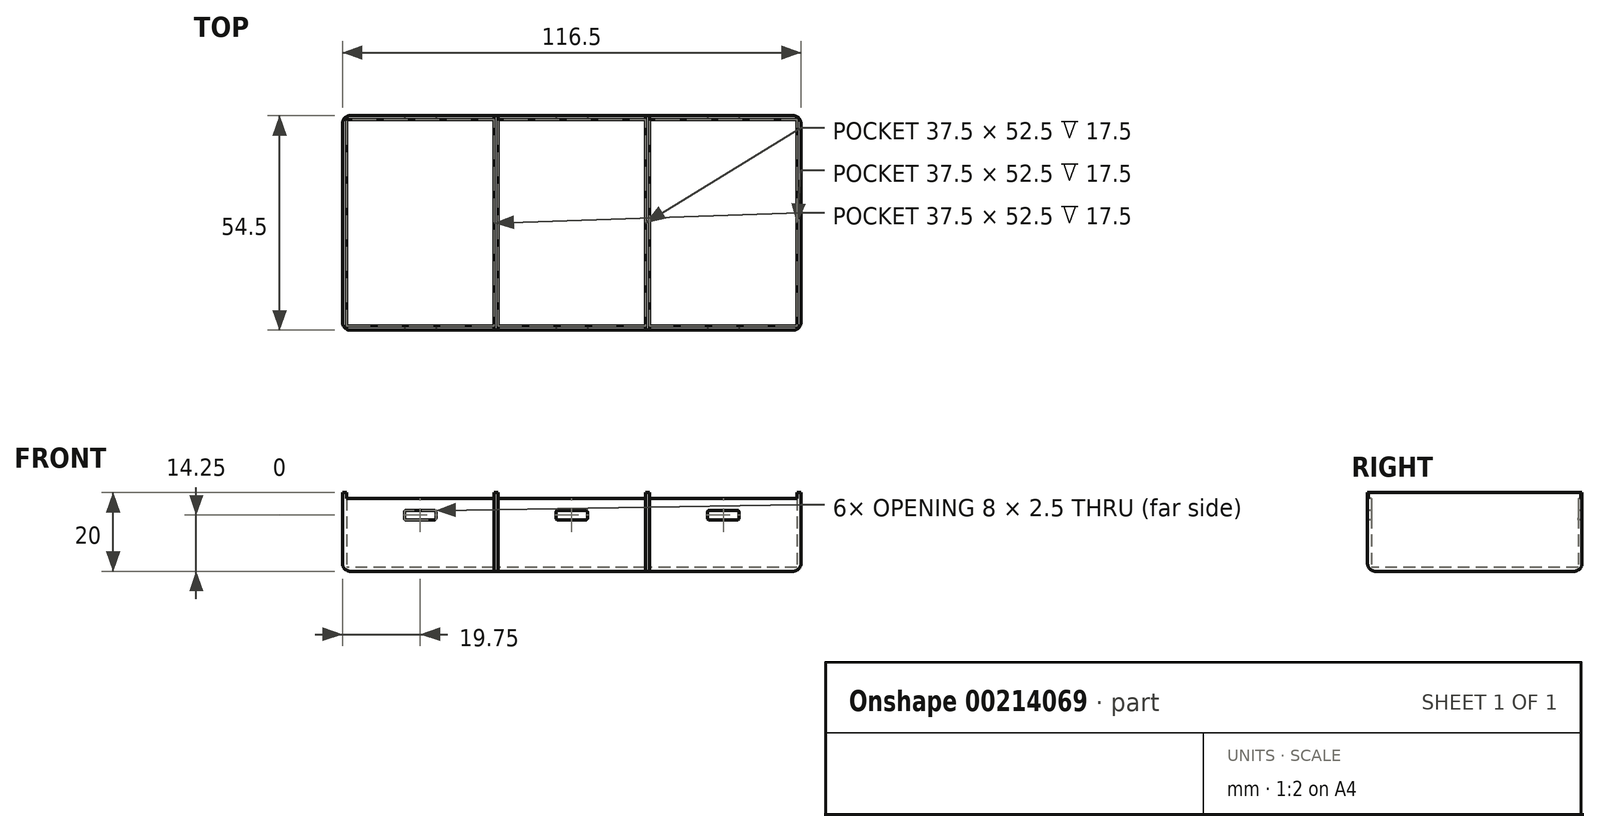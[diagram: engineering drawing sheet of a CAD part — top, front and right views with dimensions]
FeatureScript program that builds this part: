
annotation { "Feature Type Name" : "Feature", "Feature Type Description" : "" }
export const myFeature = defineFeature(function(context is Context, id is Id, definition is map)
    precondition{}
    {
        {
            var Q0;
            Q0=qCreatedBy(makeId("Top.planeOp"),FACE);
            var sketch = newSketch(context, id + "F0", { "sketchPlane" : qUnion([Q0])});
            skLineSegment(sketch, "E0.bottom", {"start": v(18.75, 26.25) * mm, "end": v(-18.75, 26.25) * mm});
            skLineSegment(sketch, "E0.top", {"start": v(18.75, -26.25) * mm, "end": v(-18.75, -26.25) * mm});
            skLineSegment(sketch, "E0.left", {"start": v(18.75, 26.25) * mm, "end": v(18.75, -26.25) * mm});
            skLineSegment(sketch, "E0.right", {"start": v(-18.75, 26.25) * mm, "end": v(-18.75, -26.25) * mm});
            skPoint(sketch, "E0.middle", {"position": v(0, 0) * mm});
            skLineSegment(sketch, "E1.bottom", {"start": v(19.75, 27.25) * mm, "end": v(-19.75, 27.25) * mm});
            skLineSegment(sketch, "E1.top", {"start": v(19.75, -27.25) * mm, "end": v(-19.75, -27.25) * mm});
            skLineSegment(sketch, "E1.left", {"start": v(19.75, 27.25) * mm, "end": v(19.75, -27.25) * mm});
            skLineSegment(sketch, "E1.right", {"start": v(-19.75, 27.25) * mm, "end": v(-19.75, -27.25) * mm});
            skLineSegment(sketch, "E2", {"start": v(18.75, 26.25) * mm, "end": v(18.75, 27.25) * mm});
            skLineSegment(sketch, "E3", {"start": v(18.75, -26.25) * mm, "end": v(18.75, -27.25) * mm});
            skLineSegment(sketch, "E4", {"start": v(-18.75, 26.25) * mm, "end": v(-18.75, 27.25) * mm});
            skLineSegment(sketch, "E5", {"start": v(-18.75, -26.25) * mm, "end": v(-18.75, -27.25) * mm});
            skSolve(sketch);
        }
        {
            var Q0;
            Q0=makeQuery(id+"F0.imprint","IMPRINT",FACE,{"disambiguationData":[TD([[makeQuery(id+"F0.imprint","IMPRINT",EDGE,{"derivedFrom":sQuery(id+"F0.wireOp",EDGE,"E0.bottom")}),1.0]])]});
            extrude(context, id + "F1", {"entities" : qUnion([Q0]), "depth" : 1 * mm});
        }
        {
            var Q0;
            Q0=makeQuery(id+"F0.imprint","IMPRINT",FACE,{"disambiguationData":[TD([[makeQuery(id+"F0.imprint","IMPRINT",EDGE,{"derivedFrom":sQuery(id+"F0.wireOp",EDGE,"E0.bottom")}),-1.0]])]});
            var Q1;
            Q1=makeQuery(id+"F0.imprint","IMPRINT",FACE,{"disambiguationData":[TD([[makeQuery(id+"F0.imprint","IMPRINT",EDGE,{"derivedFrom":sQuery(id+"F0.wireOp",EDGE,"E0.top")}),1.0]])]});
            extrude(context, id + "F2", {"entities" : qUnion([Q0, Q1]), "operationType" : NewBodyOperationType.ADD, "depth" : 18.5 * mm});
        }
        {
            var Q0;
            Q0=makeQuery(id+"F2.opExtrude","SWEPT_FACE",FACE,{"disambiguationData":[OSD([sQuery(id+"F0.wireOp",EDGE,"E1.top")])]});
            var sketch = newSketch(context, id + "F3", { "sketchPlane" : qUnion([Q0])});
            skLineSegment(sketch, "E6.bottom", {"start": v(3.5, 15.5) * mm, "end": v(-3.5, 15.5) * mm});
            skLineSegment(sketch, "E6.top", {"start": v(3.5, 13) * mm, "end": v(-3.5, 13) * mm});
            skLineSegment(sketch, "E6.left", {"start": v(4, 15) * mm, "end": v(4, 13.5) * mm});
            skLineSegment(sketch, "E6.right", {"start": v(-4, 15) * mm, "end": v(-4, 13.5) * mm});
            skPoint(sketch, "E6.middle", {"position": v(0, 14.25) * mm});
            skPoint(sketch, "E7.visualSharp", {"position": v(-4, 15.5) * mm});
            skArc(sketch, "E7.filletArc", {"start": v(-3.5, 15.5) * mm, "mid": v(-3.85, 15.35) * mm, "end": v(-4, 15) * mm});
            skPoint(sketch, "E8.visualSharp", {"position": v(-4, 13) * mm});
            skArc(sketch, "E8.filletArc", {"start": v(-4, 13.5) * mm, "mid": v(-3.85, 13.15) * mm, "end": v(-3.5, 13) * mm});
            skPoint(sketch, "E9.visualSharp", {"position": v(4, 13) * mm});
            skArc(sketch, "E9.filletArc", {"start": v(3.5, 13) * mm, "mid": v(3.85, 13.15) * mm, "end": v(4, 13.5) * mm});
            skPoint(sketch, "E10.visualSharp", {"position": v(4, 15.5) * mm});
            skArc(sketch, "E10.filletArc", {"start": v(4, 15) * mm, "mid": v(3.85, 15.35) * mm, "end": v(3.5, 15.5) * mm});
            skSolve(sketch);
        }
        {
            var Q0;
            Q0=makeQuery(id+"F3.imprint","IMPRINT",FACE,{"disambiguationData":[TD([[makeQuery(id+"F3.imprint","IMPRINT",EDGE,{"derivedFrom":sQuery(id+"F3.wireOp",EDGE,"E6.bottom")}),1.0]])]});
            extrude(context, id + "F4", {"entities" : qUnion([Q0]), "operationType" : NewBodyOperationType.REMOVE, "oppositeDirection" : true, "depth" : 60 * mm});
        }
        {
            var Q0;
            Q0=makeQuery(id+"F0.imprint","IMPRINT",FACE,{"disambiguationData":[TD([[makeQuery(id+"F0.imprint","IMPRINT",EDGE,{"derivedFrom":sQuery(id+"F0.wireOp",EDGE,"E0.right")}),-1.0]])]});
            var Q1;
            Q1=makeQuery(id+"F0.imprint","IMPRINT",FACE,{"disambiguationData":[TD([[makeQuery(id+"F0.imprint","IMPRINT",EDGE,{"derivedFrom":sQuery(id+"F0.wireOp",EDGE,"E0.left")}),1.0]])]});
            extrude(context, id + "F5", {"entities" : qUnion([Q0, Q1]), "operationType" : NewBodyOperationType.ADD, "depth" : 20 * mm});
        }
        {
            var Q0;
            Q0=makeQuery(id+"F1.opExtrude","SWEPT_BODY",BODY,{"disambiguationData":[OSD([sQuery(id+"F0.wireOp",EDGE,"E0.bottom"),sQuery(id+"F0.wireOp",EDGE,"E0.top"),sQuery(id+"F0.wireOp",EDGE,"E0.left"),sQuery(id+"F0.wireOp",EDGE,"E0.right")])]});
            transform(context, id + "F6", {"entities" : qUnion([Q0]), "transformType" : TransformType.TRANSLATION_3D, "dx" : 38.5 * mm, "dy" : 0 * mm, "dz" : 0 * mm, "makeCopy" : true});
        }
        {
            var Q0;
            Q0=makeQuery(id+"F6.opPattern","COPY",BODY,{"derivedFrom":makeQuery(id+"F1.opExtrude","SWEPT_BODY",BODY,{"disambiguationData":[OSD([sQuery(id+"F0.wireOp",EDGE,"E0.bottom"),sQuery(id+"F0.wireOp",EDGE,"E0.top"),sQuery(id+"F0.wireOp",EDGE,"E0.left"),sQuery(id+"F0.wireOp",EDGE,"E0.right")])]}),"instanceName":"1"});
            transform(context, id + "F7", {"entities" : qUnion([Q0]), "transformType" : TransformType.TRANSLATION_3D, "dx" : 38.5 * mm, "dy" : 0 * mm, "dz" : 0 * mm, "makeCopy" : true});
        }
        {
            var Q0;
            Q0=makeQuery(id+"F5.opExtrude","SWEPT_EDGE",EDGE,{"disambiguationData":[OSD([sQuery(id+"F0.wireOp",EDGE,"E1.top"),sQuery(id+"F0.wireOp",EDGE,"E1.right")])]});
            var Q1;
            Q1=makeQuery(id+"F5.opExtrude","SWEPT_EDGE",EDGE,{"disambiguationData":[OSD([sQuery(id+"F0.wireOp",EDGE,"E1.bottom"),sQuery(id+"F0.wireOp",EDGE,"E1.right")])]});
            var Q2;
            Q2=makeQuery(id+"F7.opPattern","COPY",EDGE,{"derivedFrom":makeQuery(id+"F6.opPattern","COPY",EDGE,{"derivedFrom":makeQuery(id+"F5.opExtrude","SWEPT_EDGE",EDGE,{"disambiguationData":[OSD([sQuery(id+"F0.wireOp",EDGE,"E1.top"),sQuery(id+"F0.wireOp",EDGE,"E1.left")])]}),"instanceName":"1"}),"instanceName":"1"});
            var Q3;
            Q3=makeQuery(id+"F7.opPattern","COPY",EDGE,{"derivedFrom":makeQuery(id+"F6.opPattern","COPY",EDGE,{"derivedFrom":makeQuery(id+"F5.opExtrude","SWEPT_EDGE",EDGE,{"disambiguationData":[OSD([sQuery(id+"F0.wireOp",EDGE,"E1.bottom"),sQuery(id+"F0.wireOp",EDGE,"E1.left")])]}),"instanceName":"1"}),"instanceName":"1"});
            fillet(context, id + "F8", {"entities" : qUnion([Q0, Q1, Q2, Q3]), "radius" : 2 * mm, "tangentPropagation" : true, "allowEdgeOverflow" : false});
        }
        {
            var Q0;
            {var subQ0=sQuery(id+"F0.wireOp",EDGE,"E1.top");Q0=makeQuery(id+"F5.boolean.opBoolean","MERGE",EDGE,{"derivedFrom":[makeQuery(id+"F2.opExtrude","CAP_EDGE",EDGE,{"disambiguationData":[OSD([subQ0])],"isStart":true}),makeQuery(id+"F5.opExtrude","CAP_EDGE",EDGE,{"disambiguationData":[OSD([subQ0]),TDD([makeQuery(id+"F0.imprint","IMPRINT",EDGE,{"disambiguationData":[TD([[makeQuery(id+"F0.imprint","INTERSECT",VERTEX,{"derivedFrom":[subQ0,sQuery(id+"F0.wireOp",EDGE,"E1.left")]}),-1.0]])],"derivedFrom":subQ0})])],"isStart":true}),makeQuery(id+"F5.opExtrude","CAP_EDGE",EDGE,{"disambiguationData":[OSD([subQ0]),TDD([makeQuery(id+"F0.imprint","IMPRINT",EDGE,{"disambiguationData":[TD([[makeQuery(id+"F0.imprint","INTERSECT",VERTEX,{"derivedFrom":[subQ0,sQuery(id+"F0.wireOp",EDGE,"E1.right")]}),1.0]])],"derivedFrom":subQ0})])],"isStart":true})]});}
            var Q1;
            Q1=makeQuery(id+"F5.opExtrude","CAP_EDGE",EDGE,{"disambiguationData":[OSD([sQuery(id+"F0.wireOp",EDGE,"E1.right")])],"isStart":true});
            var Q2;
            {var subQ0=sQuery(id+"F0.wireOp",EDGE,"E1.top");Q2=makeQuery(id+"F6.opPattern","COPY",EDGE,{"derivedFrom":makeQuery(id+"F5.boolean.opBoolean","MERGE",EDGE,{"derivedFrom":[makeQuery(id+"F2.opExtrude","CAP_EDGE",EDGE,{"disambiguationData":[OSD([subQ0])],"isStart":true}),makeQuery(id+"F5.opExtrude","CAP_EDGE",EDGE,{"disambiguationData":[OSD([subQ0]),TDD([makeQuery(id+"F0.imprint","IMPRINT",EDGE,{"disambiguationData":[TD([[makeQuery(id+"F0.imprint","INTERSECT",VERTEX,{"derivedFrom":[subQ0,sQuery(id+"F0.wireOp",EDGE,"E1.left")]}),-1.0]])],"derivedFrom":subQ0})])],"isStart":true}),makeQuery(id+"F5.opExtrude","CAP_EDGE",EDGE,{"disambiguationData":[OSD([subQ0]),TDD([makeQuery(id+"F0.imprint","IMPRINT",EDGE,{"disambiguationData":[TD([[makeQuery(id+"F0.imprint","INTERSECT",VERTEX,{"derivedFrom":[subQ0,sQuery(id+"F0.wireOp",EDGE,"E1.right")]}),1.0]])],"derivedFrom":subQ0})])],"isStart":true})]}),"instanceName":"1"});}
            var Q3;
            {var subQ0=sQuery(id+"F0.wireOp",EDGE,"E1.top");Q3=makeQuery(id+"F7.opPattern","COPY",EDGE,{"derivedFrom":makeQuery(id+"F6.opPattern","COPY",EDGE,{"derivedFrom":makeQuery(id+"F5.boolean.opBoolean","MERGE",EDGE,{"derivedFrom":[makeQuery(id+"F2.opExtrude","CAP_EDGE",EDGE,{"disambiguationData":[OSD([subQ0])],"isStart":true}),makeQuery(id+"F5.opExtrude","CAP_EDGE",EDGE,{"disambiguationData":[OSD([subQ0]),TDD([makeQuery(id+"F0.imprint","IMPRINT",EDGE,{"disambiguationData":[TD([[makeQuery(id+"F0.imprint","INTERSECT",VERTEX,{"derivedFrom":[subQ0,sQuery(id+"F0.wireOp",EDGE,"E1.left")]}),-1.0]])],"derivedFrom":subQ0})])],"isStart":true}),makeQuery(id+"F5.opExtrude","CAP_EDGE",EDGE,{"disambiguationData":[OSD([subQ0]),TDD([makeQuery(id+"F0.imprint","IMPRINT",EDGE,{"disambiguationData":[TD([[makeQuery(id+"F0.imprint","INTERSECT",VERTEX,{"derivedFrom":[subQ0,sQuery(id+"F0.wireOp",EDGE,"E1.right")]}),1.0]])],"derivedFrom":subQ0})])],"isStart":true})]}),"instanceName":"1"}),"instanceName":"1"});}
            var Q4;
            {var subQ0=sQuery(id+"F0.wireOp",EDGE,"E1.bottom");Q4=makeQuery(id+"F6.opPattern","COPY",EDGE,{"derivedFrom":makeQuery(id+"F5.boolean.opBoolean","MERGE",EDGE,{"derivedFrom":[makeQuery(id+"F2.opExtrude","CAP_EDGE",EDGE,{"disambiguationData":[OSD([subQ0])],"isStart":true}),makeQuery(id+"F5.opExtrude","CAP_EDGE",EDGE,{"disambiguationData":[OSD([subQ0]),TDD([makeQuery(id+"F0.imprint","IMPRINT",EDGE,{"disambiguationData":[TD([[makeQuery(id+"F0.imprint","INTERSECT",VERTEX,{"derivedFrom":[subQ0,sQuery(id+"F0.wireOp",EDGE,"E1.left")]}),-1.0]])],"derivedFrom":subQ0})])],"isStart":true}),makeQuery(id+"F5.opExtrude","CAP_EDGE",EDGE,{"disambiguationData":[OSD([subQ0]),TDD([makeQuery(id+"F0.imprint","IMPRINT",EDGE,{"disambiguationData":[TD([[makeQuery(id+"F0.imprint","INTERSECT",VERTEX,{"derivedFrom":[subQ0,sQuery(id+"F0.wireOp",EDGE,"E1.right")]}),1.0]])],"derivedFrom":subQ0})])],"isStart":true})]}),"instanceName":"1"});}
            fillet(context, id + "F9", {"entities" : qUnion([Q0, Q1, Q2, Q3, Q4]), "radius" : 2 * mm, "tangentPropagation" : true, "allowEdgeOverflow" : false});
        }
    });
